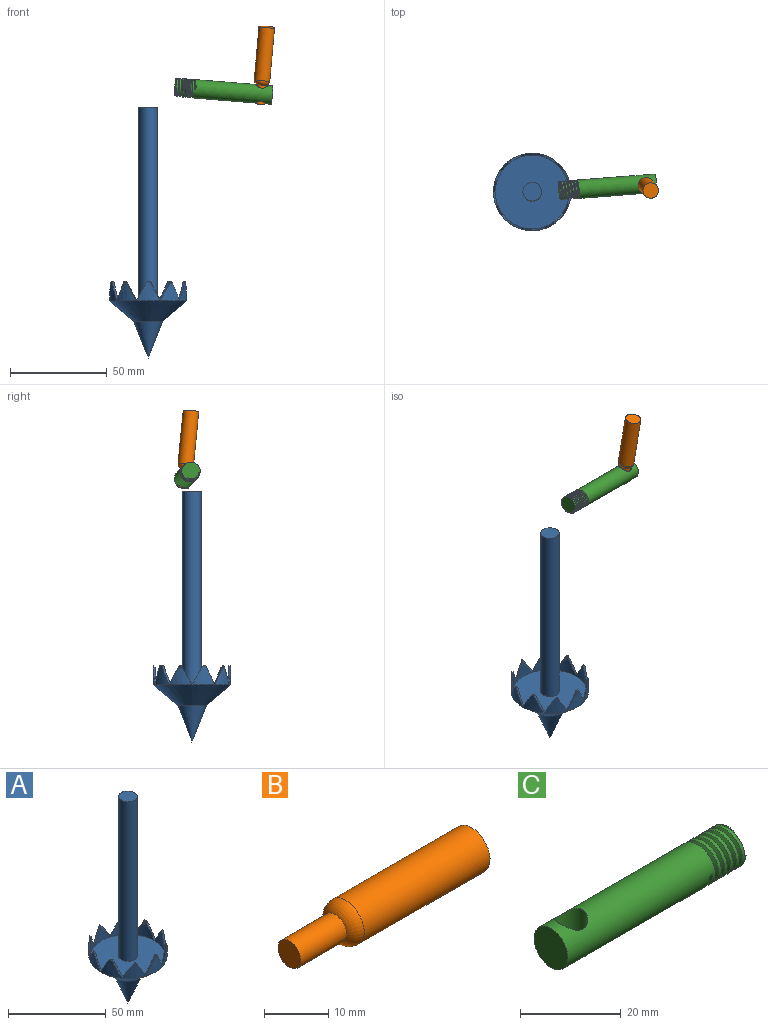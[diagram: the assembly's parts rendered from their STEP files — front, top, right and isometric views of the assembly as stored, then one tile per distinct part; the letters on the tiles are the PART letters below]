
ASSEMBLY  parts=3 mates=1
PART A: 45 faces, bbox 40x40x129.5 mm
  f0: cylinder r=20mm len=40mm, axis (0,0,-1), area 686.6mm2, adj f2,f3,f4,f5,f6,f8,f9,f10
  f1: plane 1.1x0.59mm, normal (0,0.91,0.42), area 0.2mm2, adj f5,f18,f36
  f2: plane 1.87x1.53mm, normal (0,0,1), area 1.4mm2, adj f0,f18,f39,f41
  f3: plane 0.19x0.11mm, normal (0,0,1), area 0mm2, adj f0,f4,f40
  f4: plane 9.86x6.99mm, normal (0.53,-0.73,0.42), area 14.1mm2, adj f0,f3,f18,f24,f40
  f5: plane 9.8x5.41mm, normal (0.82,-0.27,0.5), area 10.2mm2, adj f0,f1,f18,f29,f36
  f6: plane 2.64x0.75mm, normal (-0.81,-0.59,0), area 1.2mm2, adj f0,f7,f18,f27,f35
  f7: plane 1.1x0.68mm, normal (-0.86,0.28,0.42), area 0.2mm2, adj f6,f18,f35
  f8: plane 1.84x0.98mm, normal (0,0,1), area 1.4mm2, adj f0,f18,f29,f31
  f9: plane 9.8x5.34mm, normal (-0.51,0.7,0.5), area 10.4mm2, adj f0,f18,f22,f32
  f10: plane 9.47x4.97mm, normal (0,0.91,0.42), area 12.7mm2, adj f0,f18,f28,f37
  f11: plane 1.1x0.97mm, normal (0,0,1), area 0.7mm2, adj f0,f18,f21,f34
  f12: plane 1.49x1.45mm, normal (0,0,1), area 1.4mm2, adj f0,f18,f25,f28
  f13: plane 2.64x0.88mm, normal (0.31,0.95,0), area 1.2mm2, adj f0,f18,f23,f26,f38
  f14: plane 2.06x1.46mm, normal (0,0,1), area 1.4mm2, adj f0,f18,f22,f24
  f15: plane 0.19x0.12mm, normal (0,0,1), area 0mm2, adj f0,f20,f33
  f16: cone r=0mm half-angle=21.6deg, axis (0,0,1), area 479.9mm2, adj f17
  f17: cone r=20mm half-angle=49.9deg, axis (0,0,1), area 1411.2mm2, adj f0,f16
  f18: cylinder r=19.07mm len=38.14mm, axis (0,0,1), area 621.5mm2, adj f1,f2,f4,f5,f6,f7,f8,f9
  f19: plane 38.14x38.14mm, normal (0,0,1), area 1071.3mm2, adj f18,f43
  f20: plane 9.86x5.7mm, normal (0,-0.87,0.5), area 10.2mm2, adj f0,f15,f18,f21,f33
  f21: plane 9.86x5.7mm, normal (0,0.87,0.5), area 10.7mm2, adj f0,f11,f18,f20
  f22: plane 9.86x4.8mm, normal (0.51,-0.7,0.5), area 10.7mm2, adj f0,f9,f14,f18
  f23: plane 2.32x1.05mm, normal (0.53,-0.73,0.42), area 1.2mm2, adj f0,f13,f18,f42
  f24: plane 9.86x5.67mm, normal (-0.53,0.73,0.42), area 11.6mm2, adj f0,f4,f14,f18
  f25: plane 9.86x5.7mm, normal (0,0.87,0.5), area 10.7mm2, adj f0,f12,f18,f26
  f26: plane 9.8x5.66mm, normal (0,-0.87,0.5), area 10.2mm2, adj f0,f13,f18,f25,f38
  f27: plane 2.32x1.09mm, normal (0,0.91,0.42), area 1.2mm2, adj f0,f6,f18,f30
  f28: plane 9.86x4.61mm, normal (0,-0.91,0.42), area 11.6mm2, adj f0,f10,f12,f18
  f29: plane 9.86x5.97mm, normal (-0.82,0.27,0.5), area 10.7mm2, adj f0,f5,f8,f18
  f30: plane 9.47x5.58mm, normal (-0.86,0.28,0.42), area 12.7mm2, adj f0,f18,f27,f31
  f31: plane 9.86x5.51mm, normal (0.86,-0.28,0.42), area 11.6mm2, adj f0,f8,f18,f30
  f32: plane 2.64x0.88mm, normal (0.31,-0.95,0), area 1.5mm2, adj f0,f9,f18,f33
  f33: plane 2.72x1.6mm, normal (-0.86,0.28,0.42), area 2.6mm2, adj f0,f15,f18,f20,f32
  f34: plane 9.86x5.67mm, normal (-0.51,-0.7,0.5), area 10.7mm2, adj f0,f11,f18,f35
  f35: plane 9.8x4.64mm, normal (0.51,0.7,0.5), area 10.2mm2, adj f0,f6,f7,f18,f34
  f36: plane 2.64x0.75mm, normal (-0.81,0.59,0), area 1.2mm2, adj f0,f1,f5,f18,f37
  f37: plane 2.32x1.08mm, normal (0.86,0.28,0.42), area 1.2mm2, adj f0,f10,f18,f36
  f38: plane 1.1x0.6mm, normal (0.86,0.28,0.42), area 0.2mm2, adj f13,f18,f26
  f39: plane 9.86x5.45mm, normal (0.82,0.27,0.5), area 10.7mm2, adj f0,f2,f18,f40
  f40: plane 9.86x5.71mm, normal (-0.82,-0.27,0.5), area 10.2mm2, adj f0,f3,f4,f18,f39
  f41: plane 9.86x4.91mm, normal (-0.86,-0.28,0.42), area 11.6mm2, adj f0,f2,f18,f42
  f42: plane 9.47x5.86mm, normal (0.86,0.28,0.42), area 12.7mm2, adj f0,f18,f23,f41
  f43: cylinder r=4.76mm len=100mm, axis (0,0,-1), area 2992.4mm2, adj f19,f44
  f44: plane 9.53x9.53mm, normal (0,0,1), area 71.3mm2, adj f43
PART B: 5 faces, bbox 40x8.1x8.1 mm
  f0: plane 5x5mm, normal (-1,0,0), area 19.6mm2, adj f3
  f1: plane 8.06x8.06mm, normal (1,0,0), area 51mm2, adj f2
  f2: cylinder r=4.03mm len=27.62mm, axis (1,0,0), area 699.4mm2, adj f1,f4
  f3: cylinder r=2.5mm len=10.05mm, axis (1,0,0), area 157.9mm2, adj f0,f4
  f4: torus R=1.49mm, axis (-1,0,0), area 64.8mm2, adj f2,f3
PART C: 13 faces, bbox 51.4x11x12.7 mm
  f0: cylinder r=4.76mm len=42.4mm, axis (-1,0,0), area 1152.6mm2, adj f1,f7,f8,f10,f11,f12
  f1: cylinder r=4.76mm len=9.53mm, axis (-1,0,0), area 21.8mm2, adj f0,f2,f10,f11
  f2: cylinder r=4.76mm len=9.53mm, axis (-1,0,0), area 21.8mm2, adj f1,f3,f10,f11
  f3: cylinder r=4.76mm len=9.53mm, axis (-1,0,0), area 21.8mm2, adj f2,f4,f10,f11
  f4: cylinder r=4.76mm len=9.53mm, axis (-1,0,0), area 21.8mm2, adj f3,f5,f10,f11
  f5: cylinder r=4.76mm len=9.53mm, axis (-1,0,0), area 17.8mm2, adj f4,f6,f9,f10,f11
  f6: plane 9.91x9.56mm, normal (1,0,0), area 66.2mm2, adj f5,f9,f10,f11
  f7: plane 9.53x9.53mm, normal (-1,0,0), area 71.3mm2, adj f0
  f8: plane 0.94x0.81mm, normal (0,0,-1), area 0.4mm2, adj f0,f10,f11
  f9: plane 0.52x0.3mm, normal (0,0,1), area 0.1mm2, adj f5,f6,f11
  f10: bspline ~12.29x10.79mm, area 148mm2, adj f0,f1,f2,f3,f4,f5,f6,f8
  f11: bspline ~12.29x10.79mm, area 153.8mm2, adj f0,f1,f2,f3,f4,f5,f6,f8
  f12: cylinder r=3.31mm len=9.53mm, axis (0,0,1), area 197.9mm2, adj f0
PLACE A t=(0,0,-78)mm
PLACE B rot(axis=(0.09,-1,-0.01),85.4deg) t=(57.71,4.41,13.78)mm
PLACE C rot(axis=(0.04,-1,-0.05),175.2deg) t=(63.78,4.36,18.3)mm
MATE revolute B.f2 <-> C.f12  axis (0.09,-0.1,0.99) through (58.15,3.92,18.76)mm
